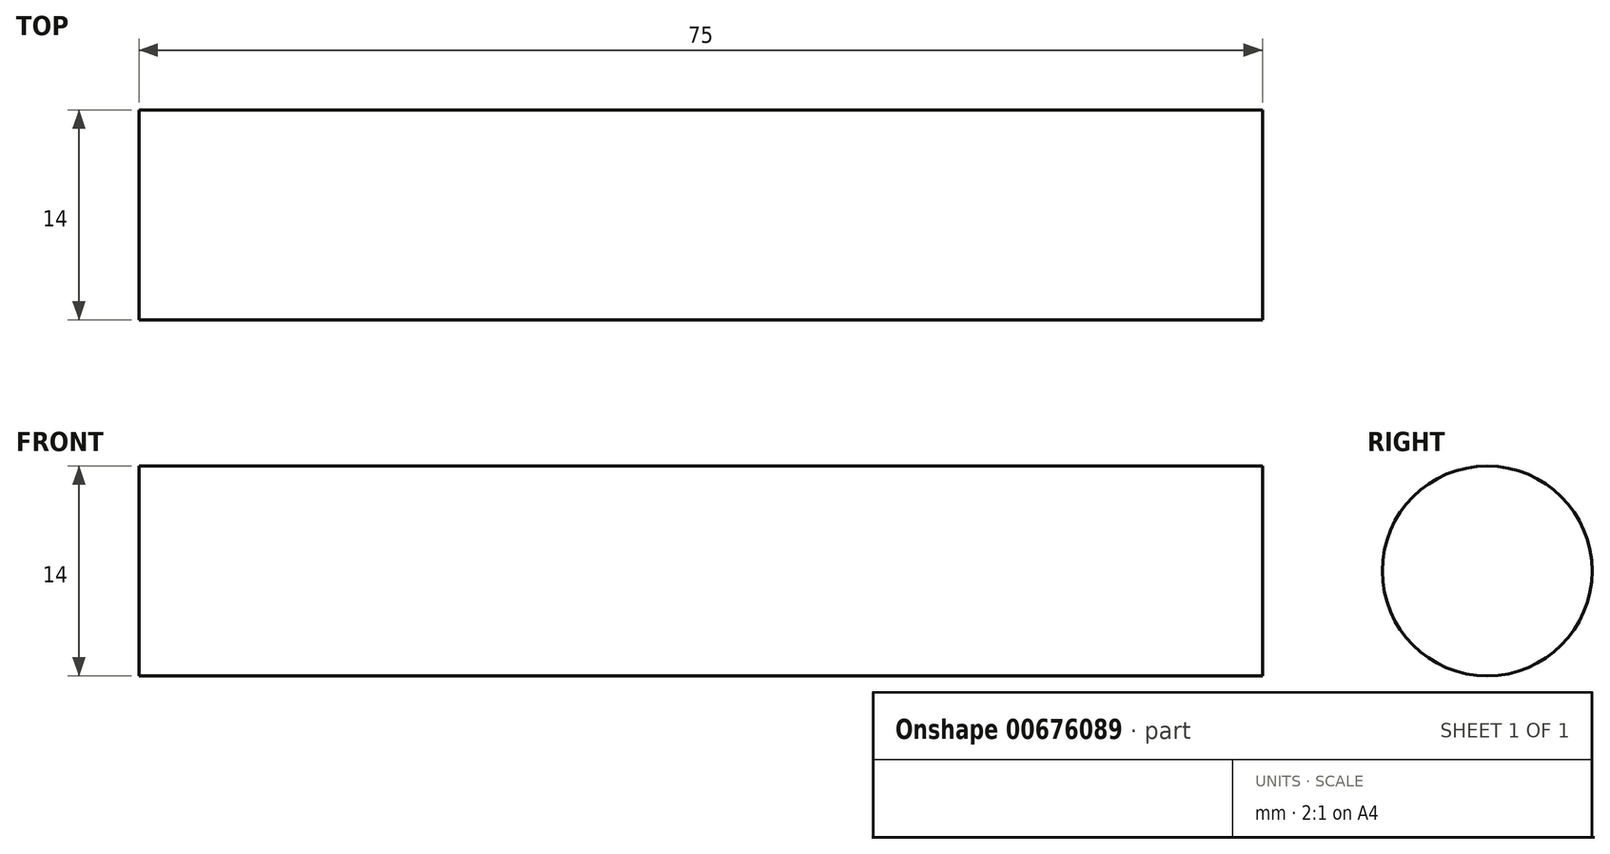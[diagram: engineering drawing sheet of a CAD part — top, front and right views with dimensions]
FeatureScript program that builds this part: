
annotation { "Feature Type Name" : "Feature", "Feature Type Description" : "" }
export const myFeature = defineFeature(function(context is Context, id is Id, definition is map)
    precondition{}
    {
        {
            var Q0;
            Q0=qCreatedBy(makeId("Right.planeOp"),FACE);
            var sketch = newSketch(context, id + "F0", { "sketchPlane" : qUnion([Q0])});
            skCircle(sketch, "E0", {"center": v(0, 0) * mm, "radius": 7 * mm});
            skSolve(sketch);
        }
        {
            var Q0;
            Q0 = qSketchRegion(id + "F0", true);
            extrude(context, id + "F1", {"entities" : qUnion([Q0]), "depth" : 75 * mm, "offsetDistance" : 25.4 * mm});
        }
    });
